# Revit family: Reece_Shower_Milli_Inox_Twin Rail Shower_Overhead with Handshower
name_source: partatom
category: Plumbing Fixtures
revit_build: Autodesk Revit 2018 (Build: 20180329_1100(x64)
units: mm (PartAtom-declared; Revit-internal decimal feet)

## family parameters
Always vertical = Yes
Cut with Voids When Loaded = Yes
Part Type = Normal
Room Calculation Point = Yes
Round Connector Dimension = Use Diameter
Shared = Yes
Work Plane-Based = Yes

## types (1)
- Brushed Stainless Steel
    Default Elevation = 0 mm  [stored 0 ft]
    Description = Milli Inox Wall Mount Twin Rail Shower with 300mm Overhead Stainless Steel (3 Star)
    Disclaimer = THIS FILE IS THE PROPERTY OF THE REECE GROUP. IT MAY NOT BE REPRODUCED, REVERSE-ENGINEERED OR MODIFIED. ANY REPUBLICATION, TRANSMISSION OR DISTRIBUTION FOR THE PURPOSE OF COMMERCIALLY EXPLOITING THE FILES IS PROHIBITED.
    Keynote = Product #2252106, Reece_Shower_Milli_Inox_Twin Rail Shower_Overhead with Handshower - Brushed Stainless Steel
    Manufacturer = Milli
    Model = Inox
    Reece_Detail_Additional = Overhead with Handshower
    Reece_Detail_Disclaimer = THIS FILE IS THE PROPERTY OF THE REECE GROUP. IT MAY NOT BE REPRODUCED, REVERSE-ENGINEERED OR MODIFIED. ANY REPUBLICATION, TRANSMISSION OR DISTRIBUTION FOR THE PURPOSE OF COMMERCIALLY EXPLOITING THE FILES IS PROHIBITED.
    Reece_Detail_Installation = Twin Rail Shower
    Reece_Material_Main = Reece_Brass_Brushed Stainless Steel
    Reece_Overall_Height = 1223 mm
    Reece_Overall_Width = 339 mm
    Reece_Product_Brand = Milli
    Reece_Product_Description = Milli Inox Wall Mount Twin Rail Shower with 300mm Overhead with Bottom Rail Water Inlet Stainless Steel (3 Star)
    Reece_Product_Mount = Wall Mounted
    Reece_Product_Number = 2252106
    Reece_Product_Sub Brand = Inox
    Reece_Product_Type = Shower
    Reece_Product_Web Page = https://www.reece.com.au
    Reece_Shower_Clearance = 370 mm
    Reece_Shower_Inlet = 13 mm
    Reece_Shower_Reach = 1083 mm
    Type Comments = Shower
    URL = https://www.reece.com.au

note: [stored X ft] marks values corroborated as IEEE doubles in the binary element streams (Revit-internal decimal feet)

## geometry (parser evidence)
native form markers: Sweep x8
no freeform markers — native parametric forms only
